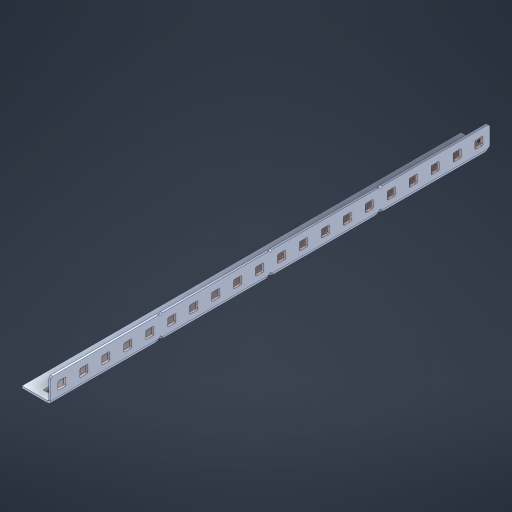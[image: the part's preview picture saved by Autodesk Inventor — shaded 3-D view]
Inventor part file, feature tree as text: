
AUTODESK INVENTOR PART (.ipt)
format: ipt  version: 2023 (Build 270158000, 158)  size: 762,368 bytes
history: native  units: in
note: dims shown in document units (in); Inventor stores cm internally (conversion verified against a paired STEP export)
features: other x45, extrude x39, sheet_metal_op x10, sketch x8, mirror x1, pattern_linear x1, chamfer x1
ambient origin geometry x8: Origin, YZ Plane, XZ Plane, XY Plane, X Axis, Y Axis, Z Axis, Center Point
bodies: Solid1 (feature_tree), Body (feature_tree)
feature tree (105):
  other  "Flange Pattern Plane"
  sheet_metal_op  "Flange Pattern"
  sheet_metal_op  "Body Pattern"
  other  "Arc Length"
  mirror  "Notch Mirror"
  pattern_linear  "Notch Pattern"  Spacing1=0.1875in  [1 undecoded]
  chamfer  "End Chamfer"
  extrude  "Half Cut"  Depth=0.0469in
  sketch  "Sketch1"  dims[d0=2.5in]
  other  "Plate1"
  sketch  "Sketch2"  dims[d1=10.0in]
  other  "Plate2"
  sheet_metal_op  "Bend1"
  sheet_metal_op  "Corner1"
  sketch  "Sketch3"  dims[d2=0.0469in]
  other  "Flange Pattern Sketch"
  sketch  "Sketch7"  dims[d3=0.0469in]
  other  "Srf1"
  other  "Srf2"
  sketch  "Sketch8"  dims[d4=0.0234in]
  sketch  "Sketch9"  dims[d5=0.0938in]
  other  "Srf91"
  sheet_metal_op  "Body Pattern Sketch"
  other  "Srf92"
  sketch  "Sketch13"  dims[d6=0.0469in]
  sketch  "Sketch14"  dims[d7=0.5in d8=90.0deg d9=0.0312in d10=0.1875in d11=0.0469in d12=0.0469in d16=0.182in d17=0.02in d18=0.0469in d19=0.0in d20=0.25in d21=0.25in d46=0.172in d47=1.0in d48=0.0in d49=0.182in d50=0.02in d51=0.25in d52=0.25in d53=0.0469in d54=0.0in d55=0.172in d56=1.0in d57=0.0in d60=7.874in d62=0.5in d63=0.3937in d65=0.5in d85=0.1227in d86=0.1659in d88=0.04in d89=0.0469in d90=0.0in d91=0.04in d92=0.0491in d95=2.5in d96=0.04in d97=0.25in d98=45.0deg d101=0.0in d102=2.497in d131=0.5in d132=7.874in d134=0.5in d139=0.5in]
  other  "Srf856"
  other  "Srf1310"
  other  "Srf1311"
  other  "Srf1312"
  other  "Srf1376"
  other  "Srf1377"
  other  "Srf1728"
  other  "Srf1755"
  other  "Srf1878"
  other  "Srf1879"
  other  "Srf1880"
  other  "Srf1881"
  other  "Srf1882"
  other  "Srf1883"
  other  "Srf1884"
  other  "Srf1885"
  other  "Srf1886"
  other  "Srf1887"
  other  "Srf1888"
  other  "Srf1889"
  other  "Srf1890"
  other  "Srf1891"
  other  "Srf1942"
  other  "Srf1943"
  other  "Srf1944"
  other  "Srf1945"
  other  "Srf1946"
  other  "Srf1947"
  other  "Srf1948"
  other  "Srf1949"
  other  "Srf1950"
  other  "Srf1951"
  other  "Srf1952"
  other  "Srf1953"
  other  "Srf1954"
  other  "Srf1955"
  sheet_metal_op  "Flange Stamp"
  sheet_metal_op  "Flange Circle"
  sheet_metal_op  "Body Stamp"
  sheet_metal_op  "Body Circle"
  sheet_metal_op  "Notch"
  extrude  "ExtrusionSrf2"  Depth=0.0469in
  extrude  "ExtrusionSrf92"  Depth=0.0469in
  extrude  "ExtrusionSrf856"  Depth=0.02in
  extrude  "ExtrusionSrf1310"  Depth=0.0469in
  extrude  "ExtrusionSrf1311"  TaperAngle=0.0deg  [1 undecoded]
  extrude  "ExtrusionSrf1312"  Depth=0.0469in
  extrude  "ExtrusionSrf1376"  Depth=0.0469in
  extrude  "ExtrusionSrf1377"  Depth=0.0469in
  extrude  "ExtrusionSrf1728"  Depth=0.0469in TaperAngle=0.0deg
  extrude  "ExtrusionSrf1755"  Depth=0.0469in
  extrude  "ExtrusionSrf1878"  Depth=0.02in
  extrude  "ExtrusionSrf1879"  Depth=0.0469in
  extrude  "ExtrusionSrf1880"  Depth=0.0469in
  extrude  "ExtrusionSrf1881"  Depth=0.0469in
  extrude  "ExtrusionSrf1882"  TaperAngle=0.0deg  [1 undecoded]
  extrude  "ExtrusionSrf1883"  Depth=0.0469in
  extrude  "ExtrusionSrf1884"  Depth=0.0469in TaperAngle=0.0deg
  extrude  "ExtrusionSrf1885"  Depth=0.0469in
  extrude  "ExtrusionSrf1886"  Depth=0.3937in
  extrude  "ExtrusionSrf1887"  Depth=0.0469in
  extrude  "ExtrusionSrf1888"  Depth=0.0469in
  extrude  "ExtrusionSrf1889"  Depth=0.0469in
  extrude  "ExtrusionSrf1890"  Depth=0.0469in
  extrude  "ExtrusionSrf1891"  TaperAngle=0.0deg  [1 undecoded]
  extrude  "ExtrusionSrf1942"  Depth=0.0469in
  extrude  "ExtrusionSrf1943"  Depth=0.0469in
  extrude  "ExtrusionSrf1944"  Depth=0.0469in
  extrude  "ExtrusionSrf1945"  Depth=0.0469in TaperAngle=45.0deg
  extrude  "ExtrusionSrf1946"  TaperAngle=0.0deg  [1 undecoded]
  extrude  "ExtrusionSrf1947"  Depth=0.0469in
  extrude  "ExtrusionSrf1948"  Depth=0.0469in
  extrude  "ExtrusionSrf1949"  Depth=0.0469in
  extrude  "ExtrusionSrf1950"  Depth=0.0469in
  extrude  "ExtrusionSrf1951"  Depth=0.0469in
  extrude  "ExtrusionSrf1952"  [1 undecoded]
  extrude  "ExtrusionSrf1953"  [1 undecoded]
  extrude  "ExtrusionSrf1954"  [1 undecoded]
  extrude  "ExtrusionSrf1955"  [1 undecoded]
note: 9 required parameter values undecoded (feature->parameter linkage not recoverable at this tier; creation-order binding heuristic only, values carry confidence <= 0.55)
